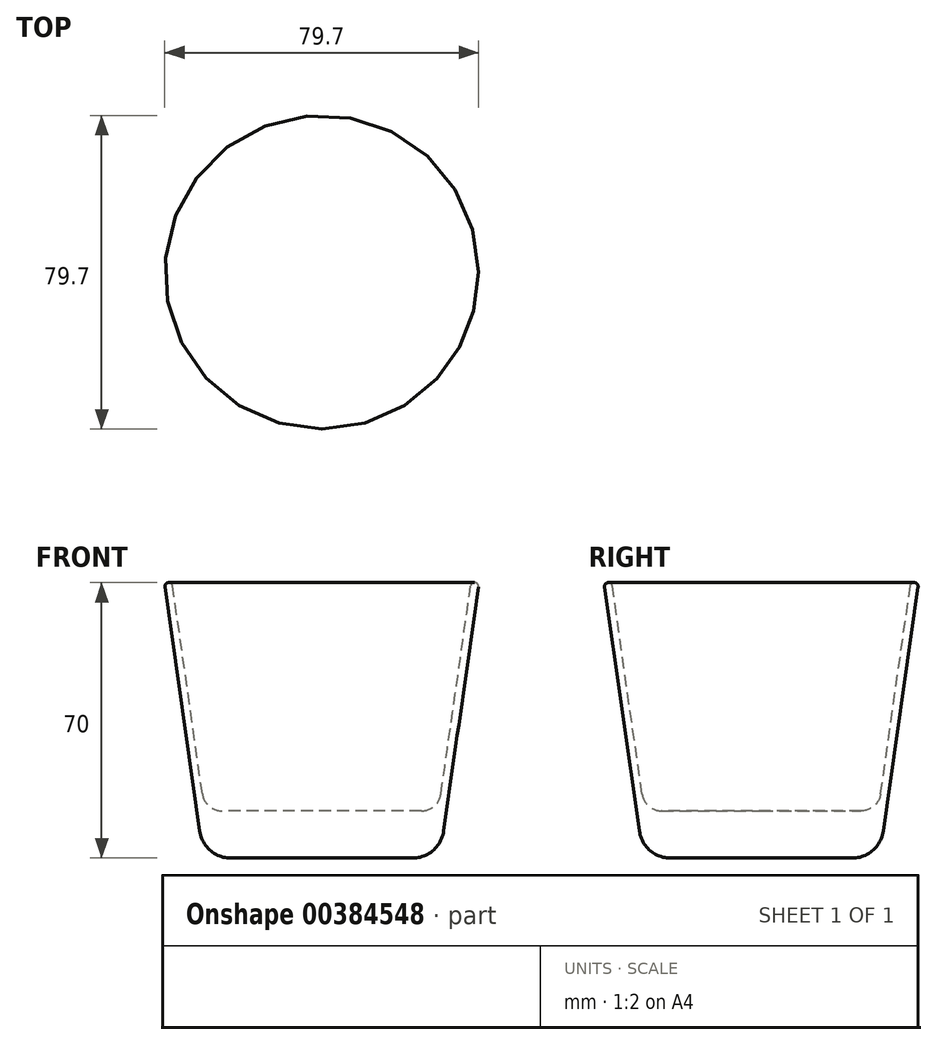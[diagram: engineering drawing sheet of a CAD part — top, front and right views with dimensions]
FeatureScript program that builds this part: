
annotation { "Feature Type Name" : "Feature", "Feature Type Description" : "" }
export const myFeature = defineFeature(function(context is Context, id is Id, definition is map)
    precondition{}
    {
        {
            var Q0;
            Q0=qCreatedBy(makeId("Front.planeOp"),FACE);
            var sketch = newSketch(context, id + "F0", { "sketchPlane" : qUnion([Q0])});
            skLineSegment(sketch, "E0", {"start": v(0, 12) * mm, "end": v(0, 0) * mm});
            skLineSegment(sketch, "E1", {"start": v(0, 0) * mm, "end": v(23.06, 0) * mm});
            skLineSegment(sketch, "E2", {"start": v(30.98, 6.87) * mm, "end": v(39.84, 68.86) * mm});
            skPoint(sketch, "E3.visualSharp", {"position": v(30, 0) * mm});
            skArc(sketch, "E3.filletArc", {"start": v(23.06, 0) * mm, "mid": v(28.3, 1.96) * mm, "end": v(30.98, 6.87) * mm});
            skLineSegment(sketch, "E4.0", {"start": v(30.3, 16.3) * mm, "end": v(37.86, 69.14) * mm});
            skLineSegment(sketch, "E5.0", {"start": v(0, 12) * mm, "end": v(25.36, 12) * mm});
            skArc(sketch, "E6.filletArc", {"start": v(25.36, 12) * mm, "mid": v(28.63, 13.22) * mm, "end": v(30.3, 16.3) * mm});
            skArc(sketch, "E7", {"start": v(39.83, 68.8) * mm, "mid": v(39.02, 69.98) * mm, "end": v(37.86, 69.14) * mm});
            skPoint(sketch, "E7.first.point", {"position": v(37.85, 69.08) * mm});
            skPoint(sketch, "E7.second.point", {"position": v(39.83, 68.8) * mm});
            skPoint(sketch, "E7.third.point", {"position": v(38.85, 70) * mm});
            skPoint(sketch, "E8.orphan", {"position": v(40, 70) * mm});
            skSolve(sketch);
        }
        {
            var Q0;
            Q0=makeQuery(id+"F0.imprint","IMPRINT",FACE,{"disambiguationData":[TD([[makeQuery(id+"F0.imprint","IMPRINT",EDGE,{"derivedFrom":sQuery(id+"F0.wireOp",EDGE,"E0")}),1.0]])]});
            var Q1;
            Q1=sQuery(id+"F0.wireOp",EDGE,"E0");
            revolve(context, id + "F1", {"entities" : qUnion([Q0]), "axis" : qUnion([Q1]), "revolveType" : RevolveType.FULL});
        }
    });
